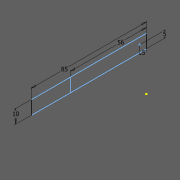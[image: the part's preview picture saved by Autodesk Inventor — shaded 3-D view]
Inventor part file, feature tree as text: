
AUTODESK INVENTOR PART (.ipt)
format: ipt  version: 2020 (Build 240168000, 168)  size: 69,632 bytes
history: native  units: in
note: dims shown in document units (in); Inventor stores cm internally (conversion verified against a paired STEP export)
features: sketch x1
ambient origin geometry x8: Origin, YZ Plane, XZ Plane, XY Plane, X Axis, Y Axis, Z Axis, Center Point
feature tree (1):
  sketch  "Sketch1"  dims[d0=0.3937in d1=3.3465in d2=0.1969in d3=2.2047in d4=0.1969in]
